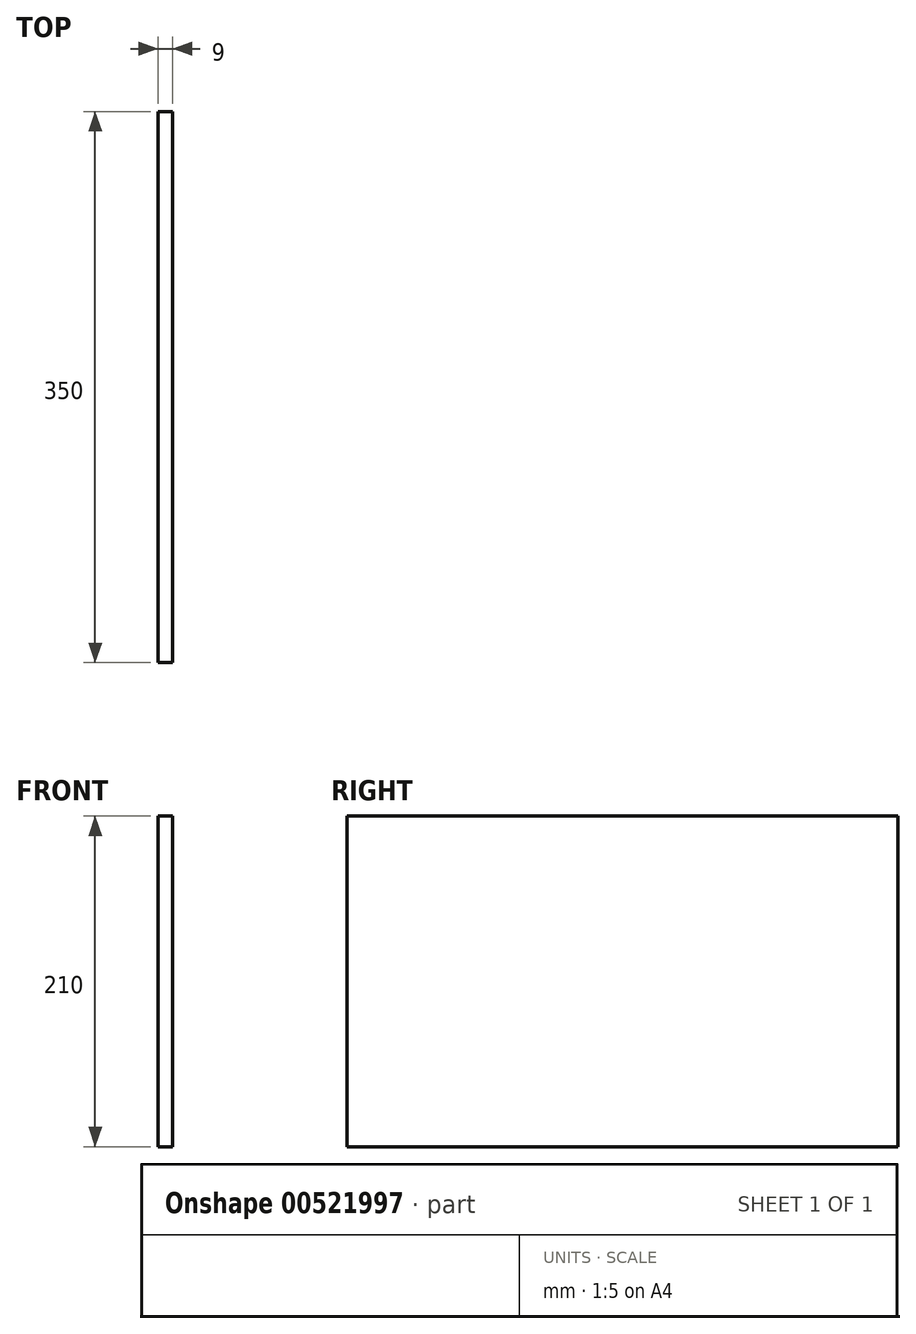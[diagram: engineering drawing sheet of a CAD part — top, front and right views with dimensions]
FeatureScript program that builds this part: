
annotation { "Feature Type Name" : "Feature", "Feature Type Description" : "" }
export const myFeature = defineFeature(function(context is Context, id is Id, definition is map)
    precondition{}
    {
        {
            var Q0;
            Q0=qCreatedBy(makeId("Right.planeOp"),FACE);
            var sketch = newSketch(context, id + "F0", { "sketchPlane" : qUnion([Q0])});
            skLineSegment(sketch, "E0.bottom", {"start": v(0, 0) * mm, "end": v(-350, 0) * mm});
            skLineSegment(sketch, "E0.top", {"start": v(0, 210) * mm, "end": v(-350, 210) * mm});
            skLineSegment(sketch, "E0.left", {"start": v(0, 0) * mm, "end": v(0, 210) * mm});
            skLineSegment(sketch, "E0.right", {"start": v(-350, 0) * mm, "end": v(-350, 210) * mm});
            skSolve(sketch);
        }
        {
            var Q0;
            Q0=makeQuery(id+"F0.imprint","IMPRINT",FACE,{"disambiguationData":[TD([[makeQuery(id+"F0.imprint","IMPRINT",EDGE,{"derivedFrom":sQuery(id+"F0.wireOp",EDGE,"E0.bottom")}),-1.0]])]});
            extrude(context, id + "F1", {"entities" : qUnion([Q0]), "depth" : 9 * mm, "offsetDistance" : 25 * mm});
        }
    });
